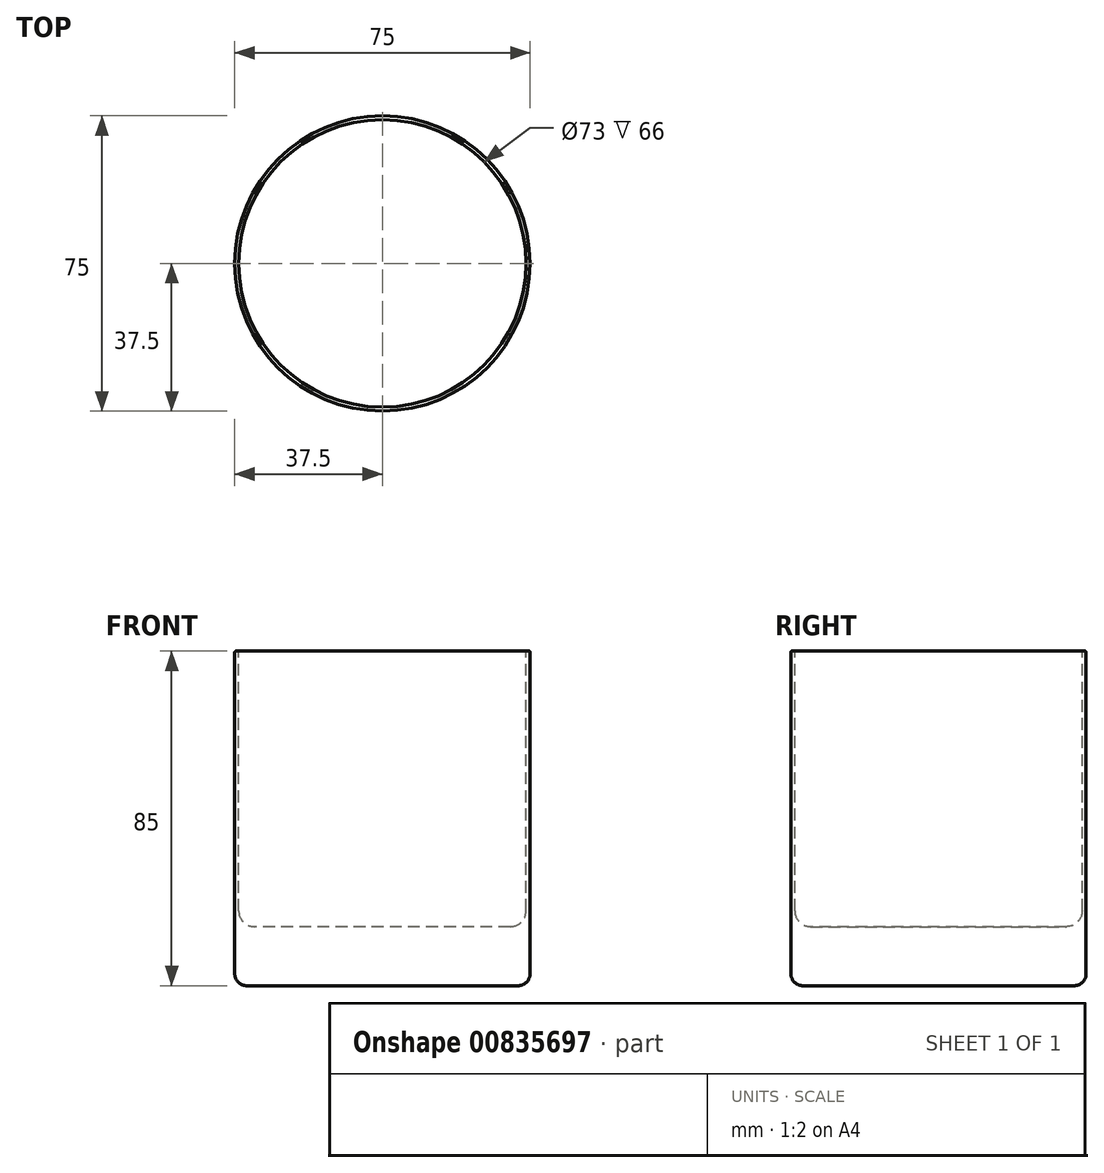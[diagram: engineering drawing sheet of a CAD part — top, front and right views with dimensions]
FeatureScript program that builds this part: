
annotation { "Feature Type Name" : "Feature", "Feature Type Description" : "" }
export const myFeature = defineFeature(function(context is Context, id is Id, definition is map)
    precondition{}
    {
        {
            var Q0;
            Q0=qCreatedBy(makeId("Top.planeOp"),FACE);
            var sketch = newSketch(context, id + "F0", { "sketchPlane" : qUnion([Q0])});
            skCircle(sketch, "E0", {"center": v(0, 0) * mm, "radius": 37.5 * mm});
            skSolve(sketch);
        }
        {
            var Q0;
            Q0=makeQuery(id+"F0.imprint","IMPRINT",FACE,{"disambiguationData":[TD([[makeQuery(id+"F0.imprint","IMPRINT",EDGE,{"derivedFrom":sQuery(id+"F0.wireOp",EDGE,"E0")}),1.0]])]});
            extrude(context, id + "F1", {"entities" : qUnion([Q0]), "depth" : 85 * mm, "offsetDistance" : 25 * mm});
        }
        {
            var Q0;
            Q0=makeQuery(id+"F1.opExtrude","CAP_FACE",FACE,{"disambiguationData":[OSD([sQuery(id+"F0.wireOp",EDGE,"E0")])],"isStart":false});
            var sketch = newSketch(context, id + "F2", { "sketchPlane" : qUnion([Q0])});
            skCircle(sketch, "E1", {"center": v(0, 0) * mm, "radius": 36.5 * mm});
            skSolve(sketch);
        }
        {
            var Q0;
            Q0=makeQuery(id+"F2.imprint","IMPRINT",FACE,{"disambiguationData":[TD([[makeQuery(id+"F2.imprint","IMPRINT",EDGE,{"derivedFrom":sQuery(id+"F2.wireOp",EDGE,"E1")}),1.0]])]});
            extrude(context, id + "F3", {"entities" : qUnion([Q0]), "operationType" : NewBodyOperationType.REMOVE, "oppositeDirection" : true, "depth" : 70 * mm, "offsetDistance" : 25 * mm});
        }
        {
            var Q0;
            Q0=makeQuery(id+"F1.opExtrude","CAP_EDGE",EDGE,{"disambiguationData":[OSD([sQuery(id+"F0.wireOp",EDGE,"E0")])],"isStart":true});
            fillet(context, id + "F4", {"entities" : qUnion([Q0]), "radius" : 3 * mm, "tangentPropagation" : true, "allowEdgeOverflow" : false});
        }
        {
            var Q0;
            Q0=makeQuery(id+"F1.opExtrude","CAP_EDGE",EDGE,{"disambiguationData":[OSD([sQuery(id+"F0.wireOp",EDGE,"E0")])],"isStart":false});
            var Q1;
            Q1=makeQuery(id+"F3.boolean.opBoolean","COPY",EDGE,{"derivedFrom":makeQuery(id+"F3.opExtrude","CAP_EDGE",EDGE,{"disambiguationData":[OSD([sQuery(id+"F2.wireOp",EDGE,"E1")])],"isStart":true})});
            fillet(context, id + "F5", {"entities" : qUnion([Q0, Q1]), "radius" : 0.25 * mm, "tangentPropagation" : true, "allowEdgeOverflow" : false});
        }
        {
            var Q0;
            Q0=makeQuery(id+"F3.boolean.opBoolean","COPY",EDGE,{"derivedFrom":makeQuery(id+"F3.opExtrude","CAP_EDGE",EDGE,{"disambiguationData":[OSD([sQuery(id+"F2.wireOp",EDGE,"E1")])],"isStart":false})});
            fillet(context, id + "F6", {"entities" : qUnion([Q0]), "radius" : 4 * mm, "tangentPropagation" : true, "allowEdgeOverflow" : false});
        }
    });
